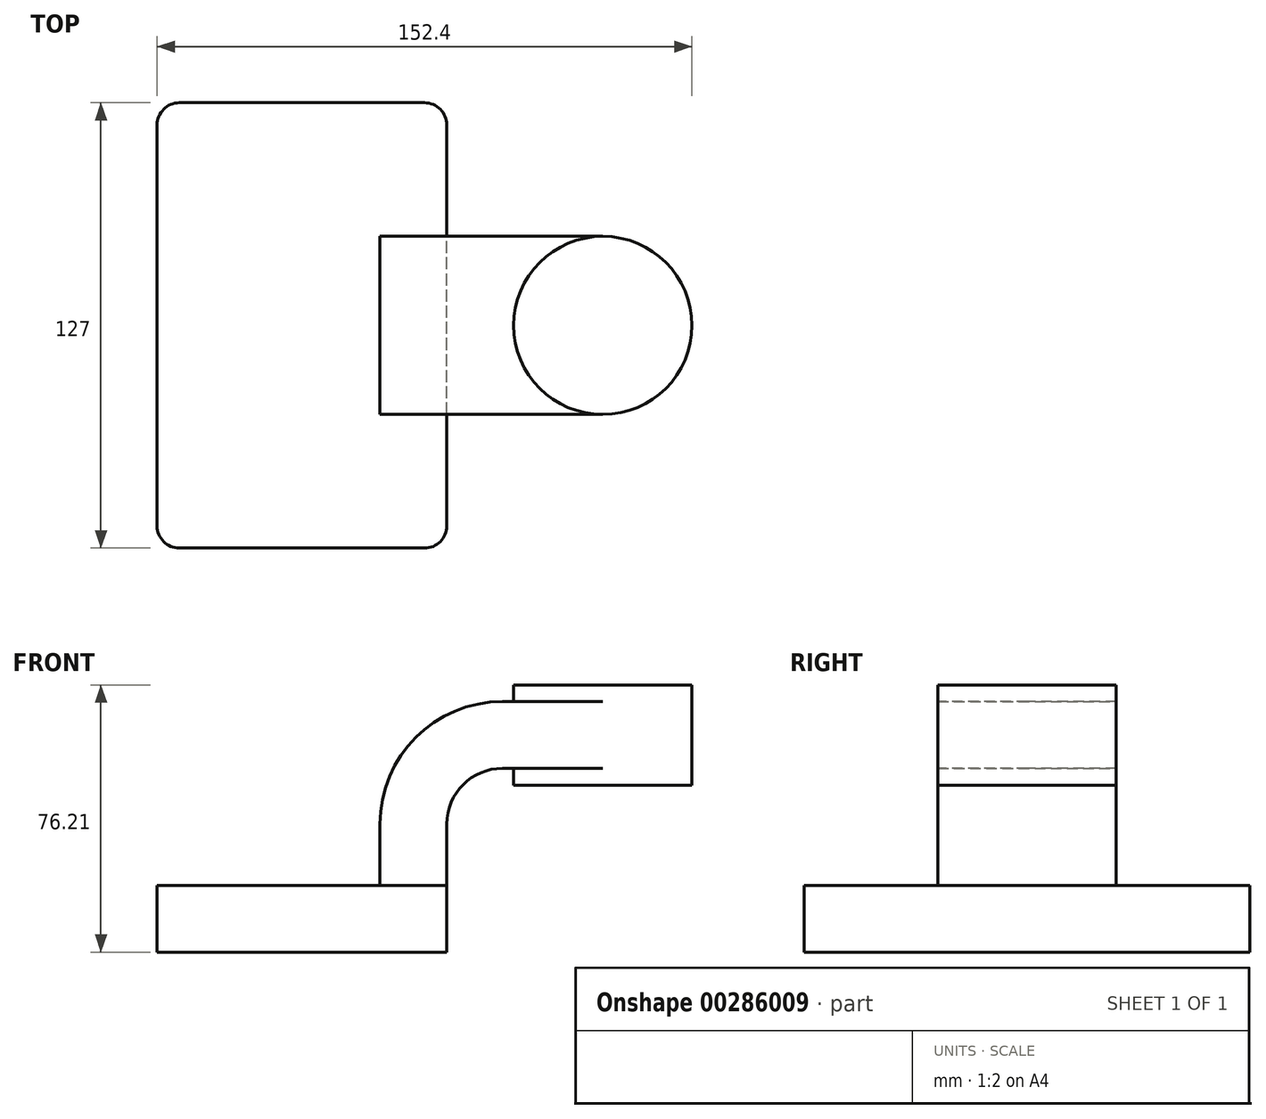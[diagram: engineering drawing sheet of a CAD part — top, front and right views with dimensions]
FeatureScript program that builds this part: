
annotation { "Feature Type Name" : "Feature", "Feature Type Description" : "" }
export const myFeature = defineFeature(function(context is Context, id is Id, definition is map)
    precondition{}
    {
        {
            var Q0;
            Q0=qCreatedBy(makeId("Front.planeOp"),FACE);
            var sketch = newSketch(context, id + "F0", { "sketchPlane" : qUnion([Q0])});
            skLineSegment(sketch, "E0.bottom", {"start": v(41.28, -9.52) * mm, "end": v(-41.27, -9.53) * mm});
            skLineSegment(sketch, "E0.top", {"start": v(41.27, 9.53) * mm, "end": v(-41.28, 9.53) * mm});
            skLineSegment(sketch, "E0.left", {"start": v(41.28, -9.52) * mm, "end": v(41.28, 9.53) * mm});
            skLineSegment(sketch, "E0.right", {"start": v(-41.27, -9.53) * mm, "end": v(-41.28, 9.53) * mm});
            skPoint(sketch, "E0.middle", {"position": v(0, 0) * mm});
            skLineSegment(sketch, "E1.bottom", {"start": v(111.12, 38.1) * mm, "end": v(60.33, 38.1) * mm});
            skLineSegment(sketch, "E1.top", {"start": v(111.12, 66.68) * mm, "end": v(60.33, 66.68) * mm});
            skLineSegment(sketch, "E1.left", {"start": v(111.12, 38.1) * mm, "end": v(111.12, 66.68) * mm});
            skLineSegment(sketch, "E1.right", {"start": v(60.33, 38.1) * mm, "end": v(60.33, 66.68) * mm});
            skPoint(sketch, "E1.middle", {"position": v(85.72, 52.39) * mm});
            skLineSegment(sketch, "E2", {"start": v(41.27, 9.53) * mm, "end": v(41.27, 27) * mm});
            skArc(sketch, "E3", {"start": v(41.27, 27) * mm, "mid": v(45.92, 38.23) * mm, "end": v(57.15, 42.88) * mm});
            skLineSegment(sketch, "E4", {"start": v(57.15, 42.88) * mm, "end": v(60.33, 42.88) * mm});
            skLineSegment(sketch, "E5.0", {"start": v(57.15, 61.93) * mm, "end": v(60.33, 61.93) * mm});
            skArc(sketch, "E5.1", {"start": v(22.23, 27) * mm, "mid": v(32.45, 51.7) * mm, "end": v(57.15, 61.93) * mm});
            skLineSegment(sketch, "E5.2", {"start": v(22.22, 9.53) * mm, "end": v(22.22, 27) * mm});
            skLineSegment(sketch, "E6", {"start": v(60.33, 42.88) * mm, "end": v(85.72, 42.88) * mm});
            skLineSegment(sketch, "E7", {"start": v(85.72, 52.39) * mm, "end": v(85.72, 66.68) * mm});
            skLineSegment(sketch, "E8", {"start": v(85.72, 52.39) * mm, "end": v(85.72, 38.1) * mm});
            skLineSegment(sketch, "E9", {"start": v(60.33, 61.93) * mm, "end": v(85.72, 61.93) * mm});
            skFitSpline(sketch, "E10", {"points": [v(-41.28, 9.52) * mm, v(57.15, 61.93) * mm], "startDerivative": vector(1.07, 62.01) * mm, "endDerivative": vector(151.24, -0.34) * mm});
            skSolve(sketch);
        }
        {
            var Q0;
            Q0=makeQuery(id+"F0.imprint","IMPRINT",FACE,{"disambiguationData":[TD([[makeQuery(id+"F0.imprint","IMPRINT",EDGE,{"derivedFrom":sQuery(id+"F0.wireOp",EDGE,"E0.bottom")}),-1.0]])]});
            extrude(context, id + "F1", {"entities" : qUnion([Q0]), "endBound" : BoundingType.SYMMETRIC, "depth" : 127 * mm});
        }
        {
            var Q0;
            {var subQ0=sQuery(id+"F0.wireOp",EDGE,"E2");Q0=makeQuery(id+"F0.imprint","IMPRINT",FACE,{"disambiguationData":[TD([[makeQuery(id+"F0.imprint","IMPRINT",EDGE,{"derivedFrom":subQ0}),1.0]])]});}
            var Q1;
            {var subQ1=sQuery(id+"F0.wireOp",EDGE,"E6");Q1=makeQuery(id+"F0.imprint","IMPRINT",FACE,{"disambiguationData":[TD([[makeQuery(id+"F0.imprint","IMPRINT",EDGE,{"derivedFrom":subQ1}),1.0]])]});}
            extrude(context, id + "F2", {"entities" : qUnion([Q0, Q1]), "endBound" : BoundingType.SYMMETRIC, "depth" : 50.8 * mm});
        }
        {
            var Q0;
            Q0=makeQuery(id+"F0.imprint","IMPRINT",FACE,{"disambiguationData":[TD([[makeQuery(id+"F0.imprint","IMPRINT",EDGE,{"derivedFrom":sQuery(id+"F0.wireOp",EDGE,"E5.1")}),1.0]])]});
            extrude(context, id + "F3", {"entities" : qUnion([Q0]), "endBound" : BoundingType.SYMMETRIC, "depth" : 15.88 * mm});
        }
        {
            var Q0;
            {var subQ0=sQuery(id+"F0.wireOp",EDGE,"E1.left");Q0=makeQuery(id+"F0.imprint","IMPRINT",FACE,{"disambiguationData":[TD([[makeQuery(id+"F0.imprint","IMPRINT",EDGE,{"derivedFrom":subQ0}),1.0]])]});}
            var Q1;
            Q1=sQuery(id+"F0.wireOp",EDGE,"E7");
            revolve(context, id + "F4", {"operationType" : NewBodyOperationType.ADD, "entities" : qUnion([Q0]), "axis" : qUnion([Q1]), "revolveType" : RevolveType.FULL});
        }
        {
            var Q0;
            Q0=makeQuery(id+"F1.opExtrude","CAP_EDGE",EDGE,{"disambiguationData":[OSD([sQuery(id+"F0.wireOp",EDGE,"E0.left")])],"isStart":false});
            var Q1;
            Q1=makeQuery(id+"F1.opExtrude","CAP_EDGE",EDGE,{"disambiguationData":[OSD([sQuery(id+"F0.wireOp",EDGE,"E0.right")])],"isStart":false});
            var Q2;
            Q2=makeQuery(id+"F1.opExtrude","CAP_EDGE",EDGE,{"disambiguationData":[OSD([sQuery(id+"F0.wireOp",EDGE,"E0.left")])],"isStart":true});
            var Q3;
            Q3=makeQuery(id+"F1.opExtrude","CAP_EDGE",EDGE,{"disambiguationData":[OSD([sQuery(id+"F0.wireOp",EDGE,"E0.right")])],"isStart":true});
            fillet(context, id + "F5", {"entities" : qUnion([Q0, Q1, Q2, Q3]), "radius" : 6.35 * mm, "tangentPropagation" : true, "allowEdgeOverflow" : false});
        }
    });
